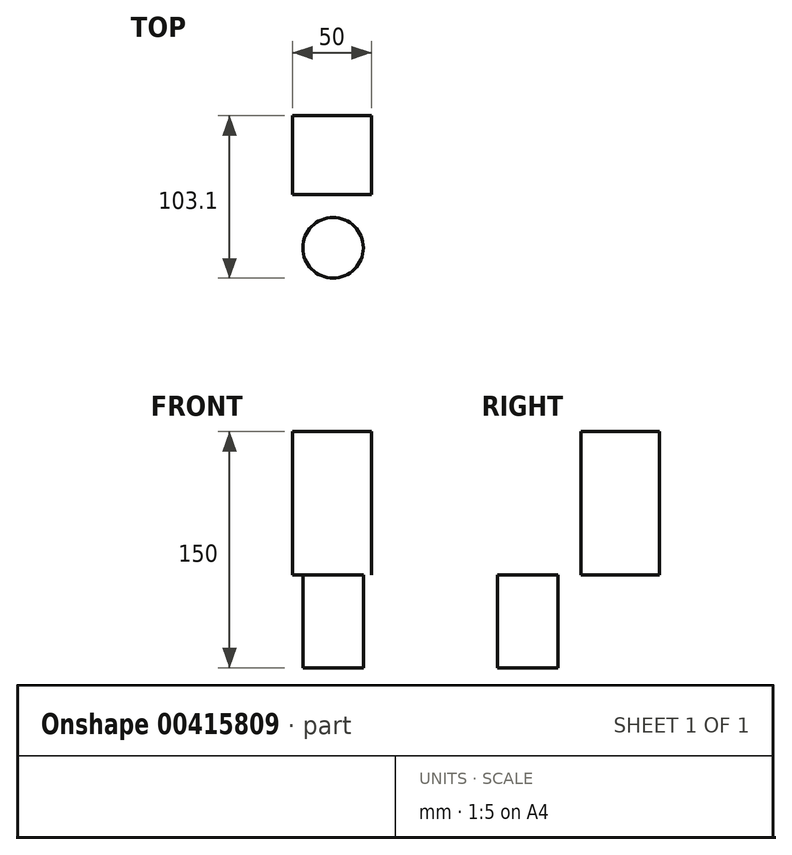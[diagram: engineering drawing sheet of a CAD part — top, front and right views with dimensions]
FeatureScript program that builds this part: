
annotation { "Feature Type Name" : "Feature", "Feature Type Description" : "" }
export const myFeature = defineFeature(function(context is Context, id is Id, definition is map)
    precondition{}
    {
        {
            var Q0;
            Q0=qCreatedBy(makeId("Top.planeOp"),FACE);
            var sketch = newSketch(context, id + "F0", { "sketchPlane" : qUnion([Q0])});
            skLineSegment(sketch, "E0.bottom", {"start": v(-75.8, 47.64) * mm, "end": v(-25.8, 47.64) * mm});
            skLineSegment(sketch, "E0.top", {"start": v(-75.8, -2.36) * mm, "end": v(-25.8, -2.36) * mm});
            skLineSegment(sketch, "E0.left", {"start": v(-75.8, 47.64) * mm, "end": v(-75.8, -2.36) * mm});
            skLineSegment(sketch, "E0.right", {"start": v(-25.8, 47.64) * mm, "end": v(-25.8, -2.36) * mm});
            skSolve(sketch);
        }
        {
            var Q0;
            Q0=makeQuery(id+"F0.imprint","IMPRINT",FACE,{"disambiguationData":[TD([[makeQuery(id+"F0.imprint","IMPRINT",EDGE,{"derivedFrom":sQuery(id+"F0.wireOp",EDGE,"E0.bottom")}),-1.0]])]});
            extrude(context, id + "F1", {"entities" : qUnion([Q0]), "depth" : 91 * mm});
        }
        {
            var Q0;
            Q0=qCreatedBy(makeId("Top.planeOp"),FACE);
            var sketch = newSketch(context, id + "F2", { "sketchPlane" : qUnion([Q0])});
            skCircle(sketch, "E1", {"center": v(-50.08, -36.26) * mm, "radius": 19.2 * mm});
            skSolve(sketch);
        }
        {
            var Q0;
            Q0=makeQuery(id+"F2.imprint","IMPRINT",FACE,{"disambiguationData":[TD([[makeQuery(id+"F2.imprint","IMPRINT",EDGE,{"derivedFrom":sQuery(id+"F2.wireOp",EDGE,"E1")}),1.0]])]});
            extrude(context, id + "F3", {"entities" : qUnion([Q0]), "oppositeDirection" : true, "depth" : 59 * mm});
        }
    });
